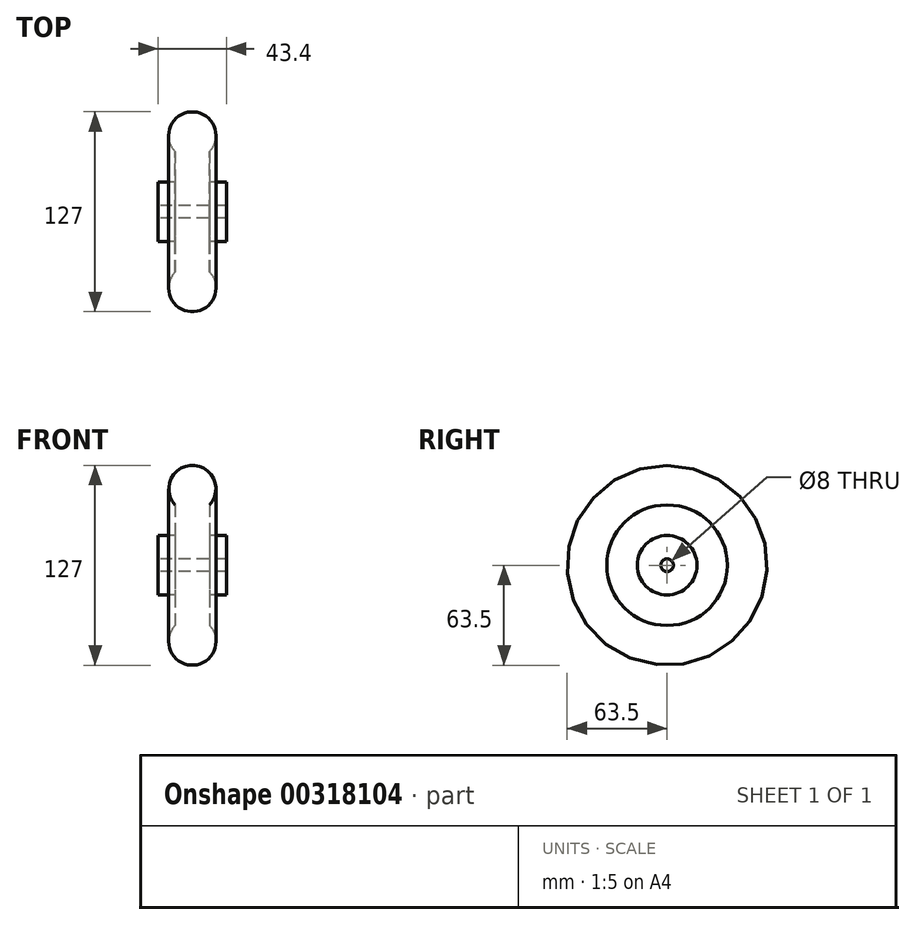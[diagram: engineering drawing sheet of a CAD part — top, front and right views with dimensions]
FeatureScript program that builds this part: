
annotation { "Feature Type Name" : "Feature", "Feature Type Description" : "" }
export const myFeature = defineFeature(function(context is Context, id is Id, definition is map)
    precondition{}
    {
        {
            var Q0;
            Q0=qCreatedBy(makeId("Front.planeOp"),FACE);
            var sketch = newSketch(context, id + "F0", { "sketchPlane" : qUnion([Q0])});
            skLineSegment(sketch, "E0", {"start": v(-21.7, 0) * mm, "end": v(21.7, 0) * mm, "construction": true});
            skLineSegment(sketch, "E1", {"start": v(-21.7, 4) * mm, "end": v(21.7, 4) * mm});
            skLineSegment(sketch, "E2", {"start": v(-21.7, 4) * mm, "end": v(-21.7, 18.92) * mm});
            skLineSegment(sketch, "E3", {"start": v(-21.7, 18.92) * mm, "end": v(-15, 18.92) * mm});
            skCircle(sketch, "E4", {"center": v(0, 48.5) * mm, "radius": 15 * mm});
            skLineSegment(sketch, "E5", {"start": v(-15, 18.92) * mm, "end": v(-11, 18.92) * mm});
            skLineSegment(sketch, "E6", {"start": v(-11, 18.92) * mm, "end": v(-11, 38.3) * mm});
            skLineSegment(sketch, "E7.MirrorCS", {"start": v(21.7, 4) * mm, "end": v(21.7, 18.92) * mm});
            skLineSegment(sketch, "E8.MirrorCS", {"start": v(21.7, 18.92) * mm, "end": v(15, 18.92) * mm});
            skLineSegment(sketch, "E9.MirrorCS", {"start": v(15, 18.92) * mm, "end": v(11, 18.92) * mm});
            skLineSegment(sketch, "E10.MirrorCS", {"start": v(11, 18.92) * mm, "end": v(11, 38.3) * mm});
            skSolve(sketch);
        }
        {
            var Q0;
            Q0 = qSketchRegion(id + "F0", true);
            var Q1;
            Q1=sQuery(id+"F0.wireOp",EDGE,"E0");
            revolve(context, id + "F1", {"entities" : qUnion([Q0]), "axis" : qUnion([Q1]), "revolveType" : RevolveType.FULL});
        }
    });
